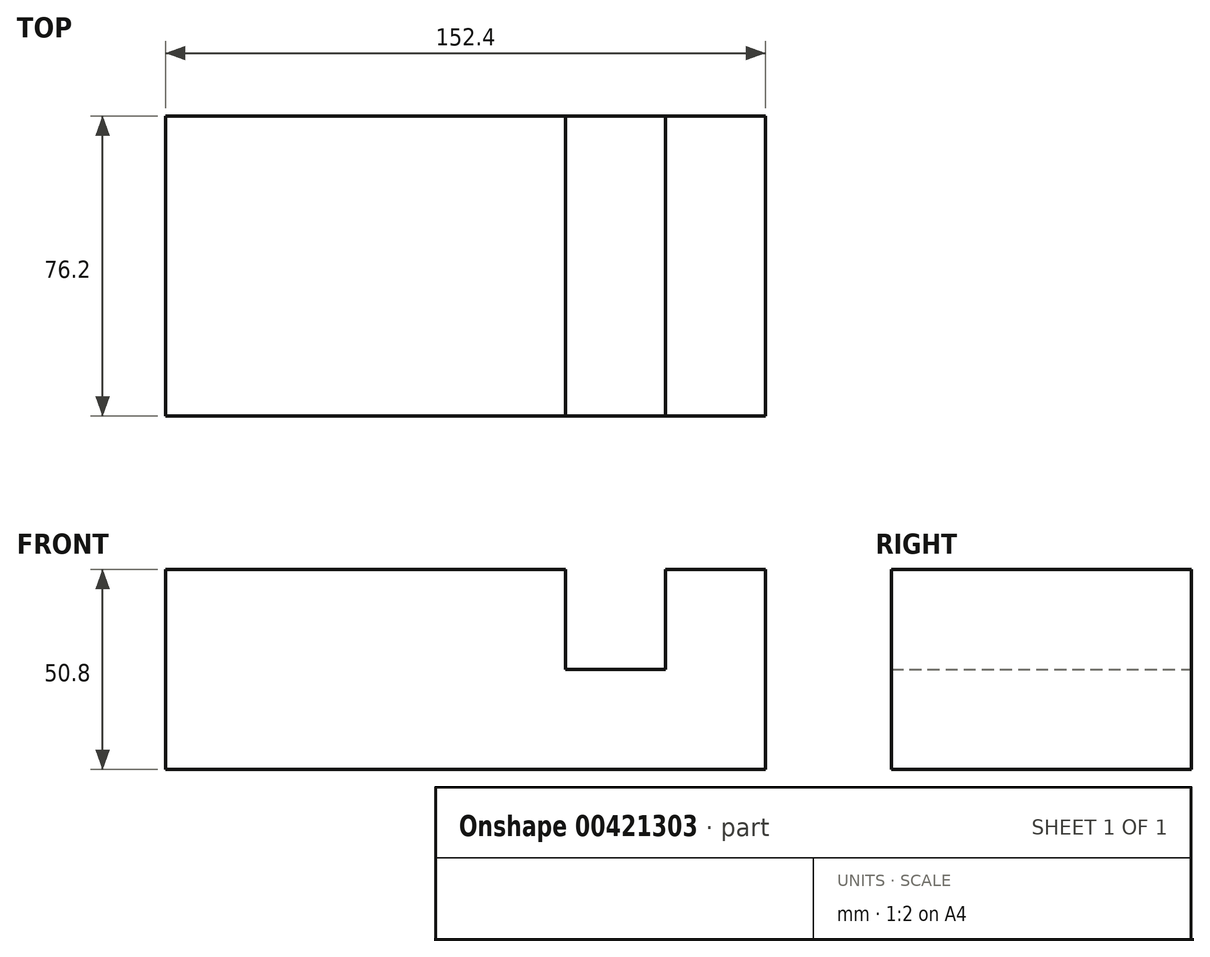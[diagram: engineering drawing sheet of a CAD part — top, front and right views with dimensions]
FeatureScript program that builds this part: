
annotation { "Feature Type Name" : "Feature", "Feature Type Description" : "" }
export const myFeature = defineFeature(function(context is Context, id is Id, definition is map)
    precondition{}
    {
        {
            var Q0;
            Q0=qCreatedBy(makeId("Front.planeOp"),FACE);
            var sketch = newSketch(context, id + "F0", { "sketchPlane" : qUnion([Q0])});
            skLineSegment(sketch, "E0", {"start": v(0, 0) * mm, "end": v(152.4, 0) * mm});
            skLineSegment(sketch, "E1", {"start": v(54.65, -120.68) * mm, "end": v(28.22, -120.68) * mm});
            skLineSegment(sketch, "E2", {"start": v(152.4, 0) * mm, "end": v(152.4, 50.8) * mm});
            skLineSegment(sketch, "E3", {"start": v(0, 0) * mm, "end": v(0, 50.8) * mm});
            skLineSegment(sketch, "E4", {"start": v(0, 50.8) * mm, "end": v(101.6, 50.8) * mm});
            skLineSegment(sketch, "E5", {"start": v(152.4, 50.8) * mm, "end": v(127, 50.8) * mm});
            skLineSegment(sketch, "E6", {"start": v(101.6, 50.8) * mm, "end": v(101.6, 25.4) * mm});
            skLineSegment(sketch, "E7", {"start": v(127, 50.8) * mm, "end": v(127, 25.4) * mm});
            skLineSegment(sketch, "E8", {"start": v(101.6, 25.4) * mm, "end": v(127, 25.4) * mm});
            skSolve(sketch);
        }
        {
            var Q0;
            Q0=makeQuery(id+"F0.imprint","IMPRINT",FACE,{"disambiguationData":[TD([[makeQuery(id+"F0.imprint","IMPRINT",EDGE,{"derivedFrom":sQuery(id+"F0.wireOp",EDGE,"E0")}),1.0]])]});
            extrude(context, id + "F1", {"entities" : qUnion([Q0]), "depth" : 76.2 * mm});
        }
    });
